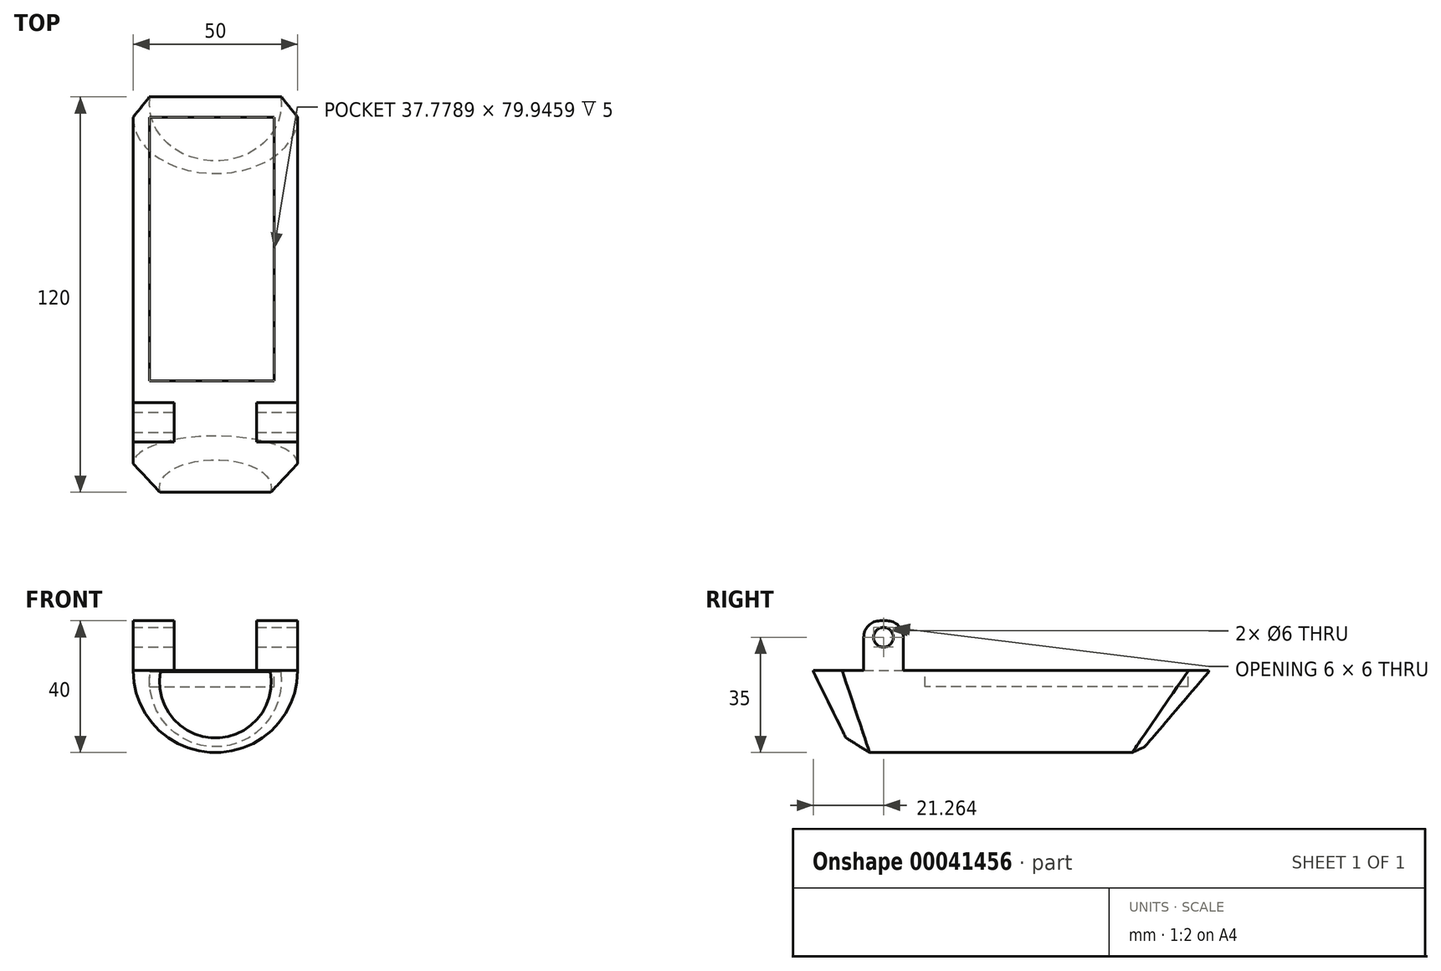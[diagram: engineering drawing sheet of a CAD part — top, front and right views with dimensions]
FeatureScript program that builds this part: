
annotation { "Feature Type Name" : "Feature", "Feature Type Description" : "" }
export const myFeature = defineFeature(function(context is Context, id is Id, definition is map)
    precondition{}
    {
        {
            var Q0;
            Q0=qCreatedBy(makeId("Top.planeOp"),FACE);
            var sketch = newSketch(context, id + "F0", { "sketchPlane" : qUnion([Q0])});
            skLineSegment(sketch, "E0.bottom", {"start": v(-25, 59.21) * mm, "end": v(0, 59.21) * mm});
            skLineSegment(sketch, "E0.top", {"start": v(-25, -60.79) * mm, "end": v(0, -60.79) * mm});
            skLineSegment(sketch, "E0.left", {"start": v(-25, 59.21) * mm, "end": v(-25, -60.79) * mm});
            skLineSegment(sketch, "E0.right", {"start": v(0, 59.21) * mm, "end": v(0, -60.79) * mm});
            skSolve(sketch);
        }
        {
            var Q0;
            Q0=makeQuery(id+"F0.imprint","IMPRINT",FACE,{"disambiguationData":[TD([[makeQuery(id+"F0.imprint","IMPRINT",EDGE,{"derivedFrom":sQuery(id+"F0.wireOp",EDGE,"E0.bottom")}),-1.0]])]});
            var Q1;
            Q1=sQuery(id+"F0.wireOp",EDGE,"E0.right");
            revolve(context, id + "F1", {"entities" : qUnion([Q0]), "axis" : qUnion([Q1]), "revolveType" : RevolveType.ONE_DIRECTION, "angle" : 180 * degree});
        }
        {
            var Q0;
            Q0=qCreatedBy(makeId("Right.planeOp"),FACE);
            cPlane(context, id + "F2", {"entities" : qUnion([Q0]), "cplaneType" : CPlaneType.OFFSET, "offset" : 25 * mm, "width" : 150 * mm, "height" : 150 * mm});
        }
        {
            var Q0;
            Q0=qCreatedBy(id+"F2.planeOp",FACE);
            var sketch = newSketch(context, id + "F3", { "sketchPlane" : qUnion([Q0])});
            skLineSegment(sketch, "E1", {"start": v(59.66, 0) * mm, "end": v(36.4, -27.19) * mm});
            skLineSegment(sketch, "E2", {"start": v(36.4, -27.19) * mm, "end": v(61.8, -26.44) * mm});
            skLineSegment(sketch, "E3", {"start": v(61.8, -26.44) * mm, "end": v(59.66, 0) * mm});
            skLineSegment(sketch, "E4", {"start": v(-61.02, 0) * mm, "end": v(-47.5, -27.43) * mm});
            skLineSegment(sketch, "E5", {"start": v(-47.5, -27.43) * mm, "end": v(-63.39, -26.32) * mm});
            skLineSegment(sketch, "E6", {"start": v(-63.39, -26.32) * mm, "end": v(-61.02, 0) * mm});
            skSolve(sketch);
        }
        {
            var Q0;
            Q0=makeQuery(id+"F3.imprint","IMPRINT",FACE,{"disambiguationData":[TD([[makeQuery(id+"F3.imprint","IMPRINT",EDGE,{"derivedFrom":sQuery(id+"F3.wireOp",EDGE,"E1")}),1.0]])]});
            var Q1;
            Q1=makeQuery(id+"F3.imprint","IMPRINT",FACE,{"disambiguationData":[TD([[makeQuery(id+"F3.imprint","IMPRINT",EDGE,{"derivedFrom":sQuery(id+"F3.wireOp",EDGE,"E4")}),-1.0]])]});
            extrude(context, id + "F4", {"entities" : qUnion([Q0, Q1]), "operationType" : NewBodyOperationType.REMOVE, "endBound" : BoundingType.THROUGH_ALL, "oppositeDirection" : true, "depth" : 25 * mm});
        }
        {
            var Q0;
            Q0=makeQuery(id+"F4.boolean.opBoolean","INTERSECT",EDGE,{"derivedFrom":[makeQuery(id+"F1.opRevolve","SWEPT_FACE",FACE,{"disambiguationData":[OSD([sQuery(id+"F0.wireOp",EDGE,"E0.left")])]}),makeQuery(id+"F4.opExtrude","SWEPT_FACE",FACE,{"disambiguationData":[OSD([sQuery(id+"F3.wireOp",EDGE,"E1")])]})]});
            chamfer(context, id + "F5", {"entities" : qUnion([Q0]), "width" : 5 * mm, "tangentPropagation" : true});
        }
        {
            var Q0;
            Q0=makeQuery(id+"F4.boolean.opBoolean","INTERSECT",EDGE,{"derivedFrom":[makeQuery(id+"F1.opRevolve","SWEPT_FACE",FACE,{"disambiguationData":[OSD([sQuery(id+"F0.wireOp",EDGE,"E0.left")])]}),makeQuery(id+"F4.opExtrude","SWEPT_FACE",FACE,{"disambiguationData":[OSD([sQuery(id+"F3.wireOp",EDGE,"E4")])]})]});
            chamfer(context, id + "F6", {"entities" : qUnion([Q0]), "width" : 8 * mm, "tangentPropagation" : true});
        }
        {
            var Q0;
            Q0=makeQuery(id+"F1.opRevolve","CAP_FACE",FACE,{"disambiguationData":[OSD([sQuery(id+"F0.wireOp",EDGE,"E0.bottom"),sQuery(id+"F0.wireOp",EDGE,"E0.top"),sQuery(id+"F0.wireOp",EDGE,"E0.left"),sQuery(id+"F0.wireOp",EDGE,"E0.right")])],"isStart":true});
            var sketch = newSketch(context, id + "F7", { "sketchPlane" : qUnion([Q0])});
            skLineSegment(sketch, "E7", {"start": v(-25, 53) * mm, "end": v(25, 53) * mm, "construction": true});
            skLineSegment(sketch, "E8", {"start": v(-20, 59.21) * mm, "end": v(-20, -60.79) * mm, "construction": true});
            skLineSegment(sketch, "E9.bottom", {"start": v(-20, 53) * mm, "end": v(17.77, 53) * mm});
            skLineSegment(sketch, "E9.top", {"start": v(-20, -26.95) * mm, "end": v(17.78, -26.95) * mm});
            skLineSegment(sketch, "E9.left", {"start": v(-20, 53) * mm, "end": v(-20, -26.95) * mm});
            skLineSegment(sketch, "E9.right", {"start": v(17.77, 53) * mm, "end": v(17.78, -26.95) * mm});
            skSolve(sketch);
        }
        {
            var Q0;
            Q0=makeQuery(id+"F7.imprint","IMPRINT",FACE,{"disambiguationData":[TD([[makeQuery(id+"F7.imprint","IMPRINT",EDGE,{"derivedFrom":sQuery(id+"F7.wireOp",EDGE,"E9.bottom")}),-1.0]])]});
            extrude(context, id + "F8", {"entities" : qUnion([Q0]), "operationType" : NewBodyOperationType.REMOVE, "oppositeDirection" : true, "depth" : 5 * mm});
        }
        {
            var Q0;
            Q0=makeQuery(id+"F1.opRevolve","CAP_FACE",FACE,{"disambiguationData":[OSD([sQuery(id+"F0.wireOp",EDGE,"E0.bottom"),sQuery(id+"F0.wireOp",EDGE,"E0.top"),sQuery(id+"F0.wireOp",EDGE,"E0.left"),sQuery(id+"F0.wireOp",EDGE,"E0.right")])],"isStart":true});
            var sketch = newSketch(context, id + "F9", { "sketchPlane" : qUnion([Q0])});
            skLineSegment(sketch, "E10.bottom", {"start": v(-25, -33.53) * mm, "end": v(-12.5, -33.53) * mm});
            skLineSegment(sketch, "E10.top", {"start": v(-25, -45.53) * mm, "end": v(-12.5, -45.53) * mm});
            skLineSegment(sketch, "E10.left", {"start": v(-25, -33.53) * mm, "end": v(-25, -45.53) * mm});
            skLineSegment(sketch, "E10.right", {"start": v(25, -33.53) * mm, "end": v(25, -45.53) * mm});
            skLineSegment(sketch, "E11.right", {"start": v(-12.5, -45.53) * mm, "end": v(-12.5, -33.53) * mm});
            skLineSegment(sketch, "E12.right", {"start": v(12.5, -45.53) * mm, "end": v(12.5, -33.53) * mm});
            skLineSegment(sketch, "E13.trimOffspring", {"start": v(12.5, -45.53) * mm, "end": v(25, -45.53) * mm});
            skPoint(sketch, "E12.bottom.start.orphan", {"position": v(0, -45.53) * mm});
            skLineSegment(sketch, "E14.trimOffspring", {"start": v(12.5, -33.53) * mm, "end": v(25, -33.53) * mm});
            skSolve(sketch);
        }
        {
            var Q0;
            Q0 = qSketchRegion(id + "F9", true);
            extrude(context, id + "F10", {"entities" : qUnion([Q0]), "operationType" : NewBodyOperationType.ADD, "depth" : 15 * mm});
        }
        {
            var Q0;
            Q0=makeQuery(id+"F10.opExtrude","CAP_EDGE",EDGE,{"disambiguationData":[OSD([sQuery(id+"F9.wireOp",EDGE,"E10.top")])],"isStart":false});
            var Q1;
            Q1=makeQuery(id+"F10.opExtrude","CAP_EDGE",EDGE,{"disambiguationData":[OSD([sQuery(id+"F9.wireOp",EDGE,"E10.bottom")])],"isStart":false});
            var Q2;
            Q2=makeQuery(id+"F10.opExtrude","CAP_EDGE",EDGE,{"disambiguationData":[OSD([sQuery(id+"F9.wireOp",EDGE,"E13.trimOffspring")])],"isStart":false});
            var Q3;
            Q3=makeQuery(id+"F10.opExtrude","CAP_EDGE",EDGE,{"disambiguationData":[OSD([sQuery(id+"F9.wireOp",EDGE,"E14.trimOffspring")])],"isStart":false});
            fillet(context, id + "F11", {"entities" : qUnion([Q0, Q1, Q2, Q3]), "radius" : 5 * mm, "tangentPropagation" : true, "allowEdgeOverflow" : false});
        }
        {
            var Q0;
            Q0=makeQuery(id+"F10.opExtrude","SWEPT_FACE",FACE,{"disambiguationData":[OSD([sQuery(id+"F9.wireOp",EDGE,"E10.right")])]});
            var sketch = newSketch(context, id + "F12", { "sketchPlane" : qUnion([Q0])});
            skCircle(sketch, "E15", {"center": v(-39.53, 10) * mm, "radius": 3 * mm});
            skPoint(sketch, "E15.centerSnap0", {"position": v(-39.53, 15) * mm});
            skSolve(sketch);
        }
        {
            var Q0;
            Q0 = qSketchRegion(id + "F12", true);
            extrude(context, id + "F13", {"entities" : qUnion([Q0]), "operationType" : NewBodyOperationType.REMOVE, "endBound" : BoundingType.THROUGH_ALL, "oppositeDirection" : true, "depth" : 25 * mm});
        }
    });
